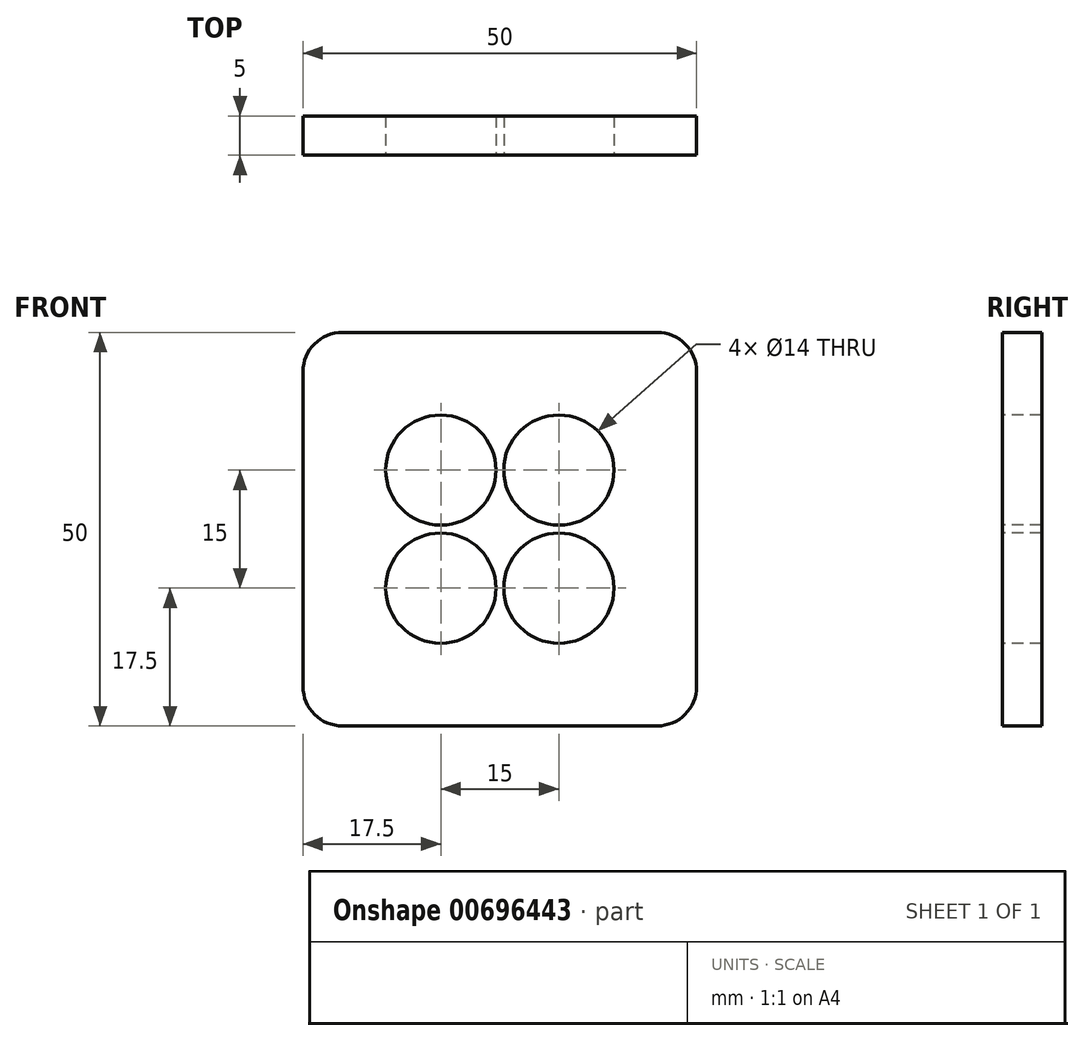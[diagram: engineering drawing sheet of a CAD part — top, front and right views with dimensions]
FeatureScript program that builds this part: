
annotation { "Feature Type Name" : "Feature", "Feature Type Description" : "" }
export const myFeature = defineFeature(function(context is Context, id is Id, definition is map)
    precondition{}
    {
        {
            var Q0;
            Q0=qCreatedBy(makeId("Front.planeOp"),FACE);
            var sketch = newSketch(context, id + "F0", { "sketchPlane" : qUnion([Q0])});
            skLineSegment(sketch, "E0.bottom", {"start": v(-45, 50) * mm, "end": v(-5, 50) * mm});
            skLineSegment(sketch, "E0.top", {"start": v(-45, 0) * mm, "end": v(-5, 0) * mm});
            skLineSegment(sketch, "E0.left", {"start": v(-50, 45) * mm, "end": v(-50, 5) * mm});
            skLineSegment(sketch, "E0.right", {"start": v(0, 45) * mm, "end": v(0, 5) * mm});
            skPoint(sketch, "E1.visualSharp", {"position": v(-50, 50) * mm});
            skArc(sketch, "E1.filletArc", {"start": v(-45, 50) * mm, "mid": v(-48.54, 48.54) * mm, "end": v(-50, 45) * mm});
            skPoint(sketch, "E2.visualSharp", {"position": v(0, 50) * mm});
            skArc(sketch, "E2.filletArc", {"start": v(0, 45) * mm, "mid": v(-1.46, 48.54) * mm, "end": v(-5, 50) * mm});
            skPoint(sketch, "E3.visualSharp", {"position": v(-50, 0) * mm});
            skArc(sketch, "E3.filletArc", {"start": v(-50, 5) * mm, "mid": v(-48.54, 1.46) * mm, "end": v(-45, 0) * mm});
            skPoint(sketch, "E4.visualSharp", {"position": v(0, 0) * mm});
            skArc(sketch, "E4.filletArc", {"start": v(-5, 0) * mm, "mid": v(-1.46, 1.46) * mm, "end": v(0, 5) * mm});
            skSolve(sketch);
        }
        {
            var Q0;
            Q0=makeQuery(id+"F0.imprint","IMPRINT",FACE,{"disambiguationData":[TD([[makeQuery(id+"F0.imprint","IMPRINT",EDGE,{"derivedFrom":sQuery(id+"F0.wireOp",EDGE,"E0.bottom")}),-1.0]])]});
            extrude(context, id + "F1", {"entities" : qUnion([Q0]), "depth" : 5 * mm, "offsetDistance" : 25 * mm});
        }
        {
            var Q0;
            Q0=makeQuery(id+"F1.opExtrude","CAP_FACE",FACE,{"disambiguationData":[OSD([sQuery(id+"F0.wireOp",EDGE,"E0.bottom"),sQuery(id+"F0.wireOp",EDGE,"E0.top"),sQuery(id+"F0.wireOp",EDGE,"E0.left"),sQuery(id+"F0.wireOp",EDGE,"E0.right"),sQuery(id+"F0.wireOp",EDGE,"E1.filletArc"),sQuery(id+"F0.wireOp",EDGE,"E2.filletArc"),sQuery(id+"F0.wireOp",EDGE,"E3.filletArc"),sQuery(id+"F0.wireOp",EDGE,"E4.filletArc")])],"isStart":false});
            var sketch = newSketch(context, id + "F2", { "sketchPlane" : qUnion([Q0])});
            skLineSegment(sketch, "E5", {"start": v(-50, 25) * mm, "end": v(0, 25) * mm, "construction": true});
            skLineSegment(sketch, "E6", {"start": v(0, 25) * mm, "end": v(-25, 50) * mm, "construction": true});
            skLineSegment(sketch, "E7", {"start": v(-25, 50) * mm, "end": v(-50, 25) * mm, "construction": true});
            skLineSegment(sketch, "E8", {"start": v(-25, 0) * mm, "end": v(0, 25) * mm, "construction": true});
            skLineSegment(sketch, "E9", {"start": v(-25, 0) * mm, "end": v(-50, 25) * mm, "construction": true});
            skLineSegment(sketch, "E10", {"start": v(-25, 25) * mm, "end": v(-25, 32.5) * mm, "construction": true});
            skLineSegment(sketch, "E11", {"start": v(-25, 32.5) * mm, "end": v(-25, 32.5) * mm});
            skLineSegment(sketch, "E12", {"start": v(-32.5, 32.5) * mm, "end": v(-25, 32.5) * mm, "construction": true});
            skLineSegment(sketch, "E13.MirrorCS", {"start": v(-17.5, 32.5) * mm, "end": v(-25, 32.5) * mm, "construction": true});
            skLineSegment(sketch, "E14.MirrorCS", {"start": v(-17.5, 17.5) * mm, "end": v(-25, 17.5) * mm, "construction": true});
            skLineSegment(sketch, "E15.MirrorCS", {"start": v(-32.5, 17.5) * mm, "end": v(-25, 17.5) * mm, "construction": true});
            skCircle(sketch, "E16", {"center": v(-17.5, 32.5) * mm, "radius": 7 * mm});
            skCircle(sketch, "E17", {"center": v(-32.5, 32.5) * mm, "radius": 7 * mm});
            skCircle(sketch, "E18", {"center": v(-17.5, 17.5) * mm, "radius": 7 * mm});
            skCircle(sketch, "E19", {"center": v(-32.5, 17.5) * mm, "radius": 7 * mm});
            skSolve(sketch);
        }
        {
            var Q0;
            Q0 = qSketchRegion(id + "F2", true);
            extrude(context, id + "F3", {"entities" : qUnion([Q0]), "operationType" : NewBodyOperationType.REMOVE, "endBound" : BoundingType.THROUGH_ALL, "oppositeDirection" : true, "depth" : 25 * mm, "offsetDistance" : 25 * mm});
        }
    });
